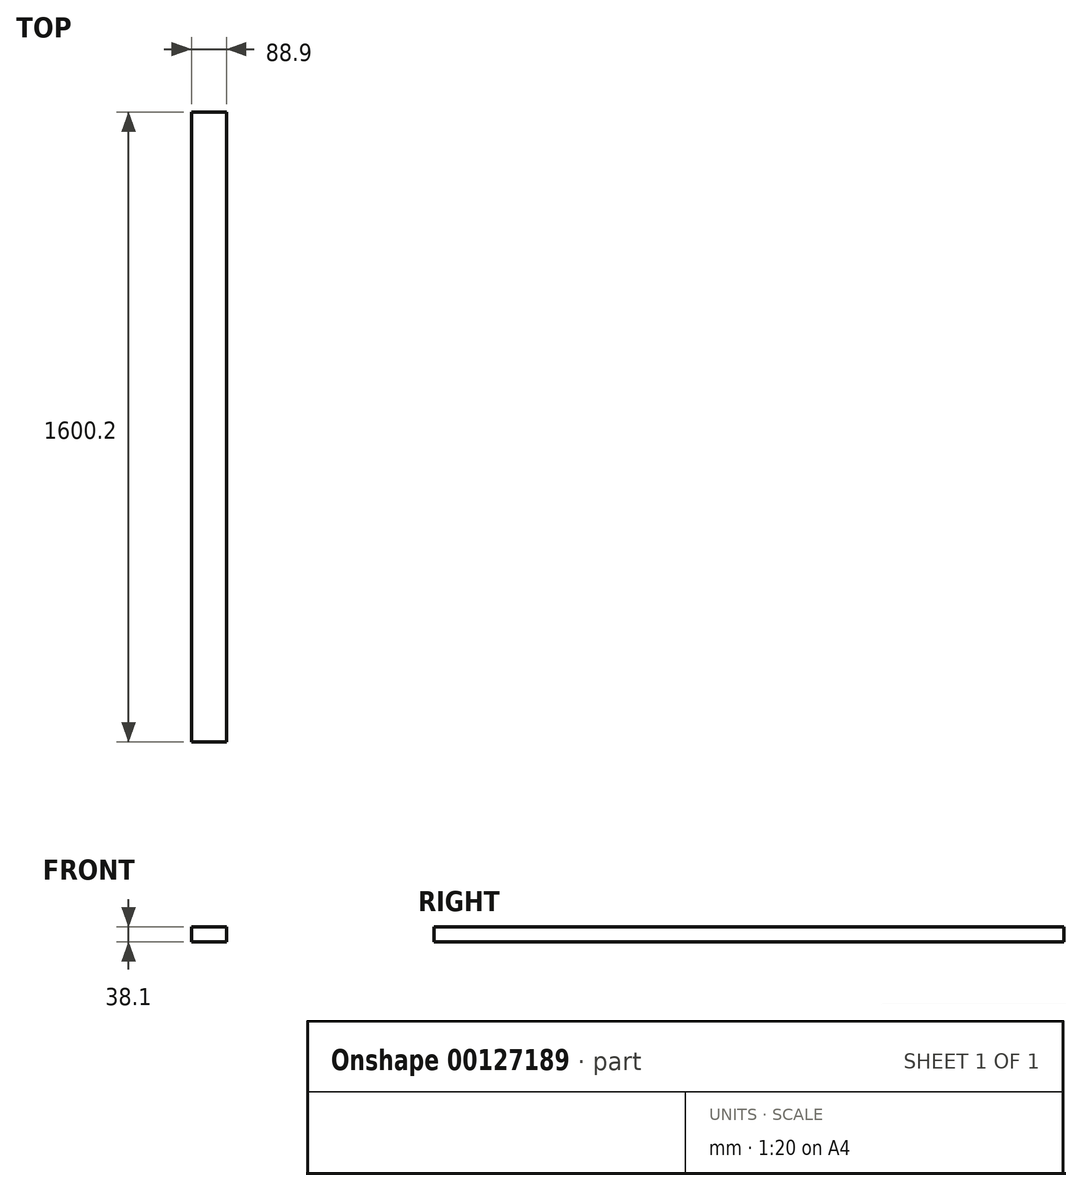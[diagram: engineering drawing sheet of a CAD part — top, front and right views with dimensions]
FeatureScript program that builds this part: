
annotation { "Feature Type Name" : "Feature", "Feature Type Description" : "" }
export const myFeature = defineFeature(function(context is Context, id is Id, definition is map)
    precondition{}
    {
        {
            var Q0;
            Q0=qCreatedBy(makeId("Front.planeOp"),FACE);
            var sketch = newSketch(context, id + "F0", { "sketchPlane" : qUnion([Q0])});
            skLineSegment(sketch, "E0.bottom", {"start": v(44.45, -19.05) * mm, "end": v(-44.45, -19.05) * mm});
            skLineSegment(sketch, "E0.top", {"start": v(44.45, 19.05) * mm, "end": v(-44.45, 19.05) * mm});
            skLineSegment(sketch, "E0.left", {"start": v(44.45, -19.05) * mm, "end": v(44.45, 19.05) * mm});
            skLineSegment(sketch, "E0.right", {"start": v(-44.45, -19.05) * mm, "end": v(-44.45, 19.05) * mm});
            skPoint(sketch, "E0.middle", {"position": v(0, 0) * mm});
            skSolve(sketch);
        }
        {
            var Q0;
            Q0=qSketchRegion(id+"F0",true);
            extrude(context, id + "F1", {"entities" : qUnion([Q0]), "depth" : 1600.2 * mm, "offsetDistance" : 25.4 * mm});
        }
    });
